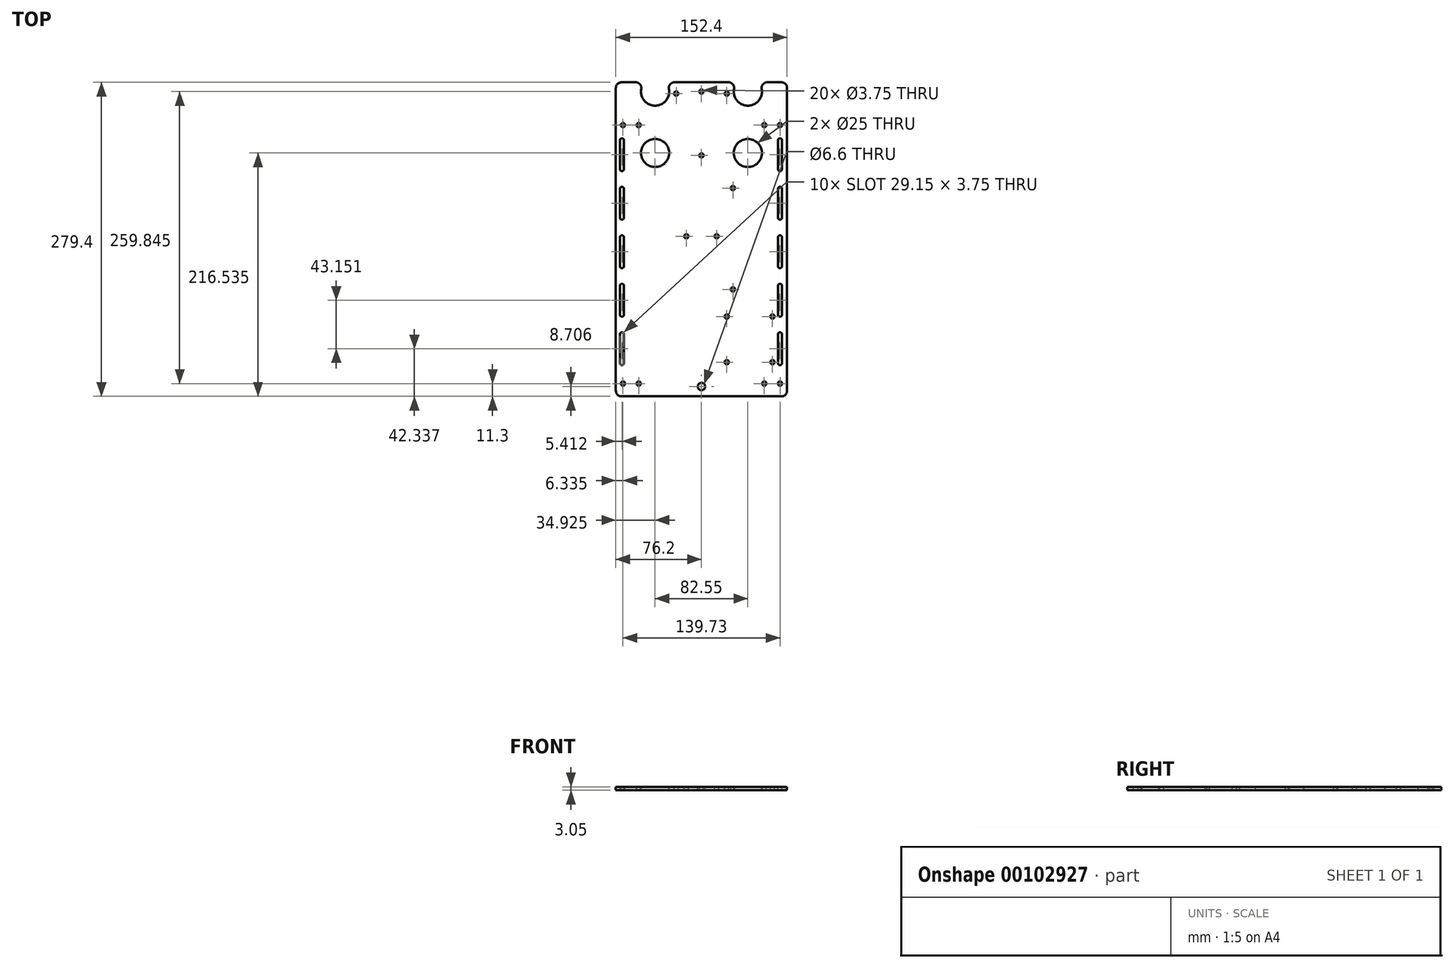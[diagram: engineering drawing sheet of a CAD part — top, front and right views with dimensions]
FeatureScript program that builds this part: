
annotation { "Feature Type Name" : "Feature", "Feature Type Description" : "" }
export const myFeature = defineFeature(function(context is Context, id is Id, definition is map)
    precondition{}
    {
        {
            var Q0;
            Q0=qCreatedBy(makeId("Top.planeOp"),FACE);
            var sketch = newSketch(context, id + "F0", { "sketchPlane" : qUnion([Q0])});
            skLineSegment(sketch, "E0.bottom", {"start": v(-76.2, 139.7) * mm, "end": v(76.2, 139.7) * mm});
            skLineSegment(sketch, "E0.top", {"start": v(-76.2, -139.7) * mm, "end": v(76.2, -139.7) * mm});
            skLineSegment(sketch, "E0.left", {"start": v(-76.2, 139.7) * mm, "end": v(-76.2, -139.7) * mm});
            skLineSegment(sketch, "E0.right", {"start": v(76.2, 139.7) * mm, "end": v(76.2, -139.7) * mm});
            skPoint(sketch, "E0.middle", {"position": v(0, 0) * mm});
            skLineSegment(sketch, "E1", {"start": v(0, 0) * mm, "end": v(0, 139.7) * mm, "construction": true});
            skLineSegment(sketch, "E2", {"start": v(-69.86, 101.6) * mm, "end": v(-55.87, 101.6) * mm, "construction": true});
            skLineSegment(sketch, "E3", {"start": v(-69.86, -128.4) * mm, "end": v(-55.86, -128.4) * mm, "construction": true});
            skLineSegment(sketch, "E4", {"start": v(27.98, 45.6) * mm, "end": v(27.98, -44.57) * mm, "construction": true});
            skLineSegment(sketch, "E5.bottom", {"start": v(-3.77, 51.31) * mm, "end": v(59.73, 51.31) * mm, "construction": true});
            skLineSegment(sketch, "E5.top", {"start": v(-3.77, -50.29) * mm, "end": v(59.73, -50.29) * mm, "construction": true});
            skLineSegment(sketch, "E5.left", {"start": v(-3.77, 51.31) * mm, "end": v(-3.77, -50.29) * mm, "construction": true});
            skLineSegment(sketch, "E5.right", {"start": v(59.73, 51.31) * mm, "end": v(59.73, -50.29) * mm, "construction": true});
            skPoint(sketch, "E5.middle", {"position": v(27.98, 0.51) * mm});
            skLineSegment(sketch, "E6.bottom", {"start": v(-68.9, 107.6) * mm, "end": v(-56.83, 107.6) * mm, "construction": true});
            skLineSegment(sketch, "E6.top", {"start": v(-68.9, 95.6) * mm, "end": v(-56.83, 95.6) * mm, "construction": true});
            skLineSegment(sketch, "E6.left", {"start": v(-68.9, 107.6) * mm, "end": v(-68.9, 95.6) * mm, "construction": true});
            skLineSegment(sketch, "E6.right", {"start": v(-56.83, 107.6) * mm, "end": v(-56.83, 95.6) * mm, "construction": true});
            skPoint(sketch, "E6.middle", {"position": v(-62.87, 101.6) * mm});
            skLineSegment(sketch, "E7.bottom", {"start": v(63.16, -109.33) * mm, "end": v(22.52, -109.33) * mm, "construction": true});
            skLineSegment(sketch, "E7.top", {"start": v(63.16, -68.7) * mm, "end": v(22.52, -68.7) * mm, "construction": true});
            skLineSegment(sketch, "E7.left", {"start": v(63.16, -109.33) * mm, "end": v(63.16, -68.7) * mm, "construction": true});
            skLineSegment(sketch, "E7.right", {"start": v(22.52, -109.33) * mm, "end": v(22.52, -68.7) * mm, "construction": true});
            skPoint(sketch, "E7.middle", {"position": v(42.84, -89.01) * mm});
            skLineSegment(sketch, "E8.MirrorCS", {"start": v(69.86, 101.6) * mm, "end": v(55.87, 101.6) * mm, "construction": true});
            skLineSegment(sketch, "E9.MirrorCS", {"start": v(69.87, -128.4) * mm, "end": v(55.87, -128.4) * mm, "construction": true});
            skLineSegment(sketch, "E10.bottom", {"start": v(-41.28, 131.44) * mm, "end": v(41.28, 131.44) * mm, "construction": true});
            skLineSegment(sketch, "E10.top", {"start": v(-41.28, 76.83) * mm, "end": v(41.27, 76.83) * mm, "construction": true});
            skLineSegment(sketch, "E10.left", {"start": v(-41.28, 131.44) * mm, "end": v(-41.28, 76.83) * mm, "construction": true});
            skLineSegment(sketch, "E10.right", {"start": v(41.28, 131.44) * mm, "end": v(41.27, 76.83) * mm, "construction": true});
            skPoint(sketch, "E10.middle", {"position": v(0, 104.14) * mm});
            skLineSegment(sketch, "E11", {"start": v(0, 131.44) * mm, "end": v(0, 74.68) * mm, "construction": true});
            skCircle(sketch, "E12", {"center": v(-41.28, 131.44) * mm, "radius": 12.5 * mm});
            skCircle(sketch, "E13", {"center": v(-41.28, 76.83) * mm, "radius": 12.5 * mm});
            skCircle(sketch, "E14", {"center": v(41.27, 76.83) * mm, "radius": 12.5 * mm});
            skCircle(sketch, "E15", {"center": v(41.28, 131.44) * mm, "radius": 12.5 * mm});
            skCircle(sketch, "E16", {"center": v(0, -131) * mm, "radius": 3.3 * mm});
            skLineSegment(sketch, "E17", {"start": v(69.85, 87.94) * mm, "end": v(69.85, 62.54) * mm, "construction": true});
            skArc(sketch, "E18.0.startCap", {"start": v(67.97, 87.94) * mm, "mid": v(69.85, 89.81) * mm, "end": v(71.72, 87.94) * mm});
            skArc(sketch, "E18.0.endCap", {"start": v(71.72, 62.54) * mm, "mid": v(69.85, 60.66) * mm, "end": v(67.97, 62.54) * mm});
            skLineSegment(sketch, "E18.0.left", {"start": v(71.72, 87.94) * mm, "end": v(71.72, 62.54) * mm});
            skLineSegment(sketch, "E18.0.right", {"start": v(67.97, 87.94) * mm, "end": v(67.97, 62.54) * mm});
            skLineSegment(sketch, "E19.0.1.0", {"start": v(71.72, 44.79) * mm, "end": v(71.72, 19.39) * mm});
            skArc(sketch, "E19.0.1.1", {"start": v(71.72, 19.39) * mm, "mid": v(69.85, 17.51) * mm, "end": v(67.97, 19.39) * mm});
            skLineSegment(sketch, "E19.0.1.2", {"start": v(67.97, 44.79) * mm, "end": v(67.97, 19.39) * mm});
            skArc(sketch, "E19.0.1.3", {"start": v(67.97, 44.79) * mm, "mid": v(69.85, 46.66) * mm, "end": v(71.72, 44.79) * mm});
            skLineSegment(sketch, "E19.0.2.0", {"start": v(71.72, 1.64) * mm, "end": v(71.72, -23.76) * mm});
            skArc(sketch, "E19.0.2.1", {"start": v(71.72, -23.76) * mm, "mid": v(69.85, -25.64) * mm, "end": v(67.97, -23.76) * mm});
            skLineSegment(sketch, "E19.0.2.2", {"start": v(67.97, 1.64) * mm, "end": v(67.97, -23.76) * mm});
            skArc(sketch, "E19.0.2.3", {"start": v(67.97, 1.64) * mm, "mid": v(69.85, 3.51) * mm, "end": v(71.72, 1.64) * mm});
            skLineSegment(sketch, "E19.0.3.0", {"start": v(71.72, -41.51) * mm, "end": v(71.72, -66.91) * mm});
            skArc(sketch, "E19.0.3.1", {"start": v(71.72, -66.91) * mm, "mid": v(69.85, -68.79) * mm, "end": v(67.97, -66.91) * mm});
            skLineSegment(sketch, "E19.0.3.2", {"start": v(67.97, -41.51) * mm, "end": v(67.97, -66.91) * mm});
            skArc(sketch, "E19.0.3.3", {"start": v(67.97, -41.51) * mm, "mid": v(69.85, -39.64) * mm, "end": v(71.72, -41.51) * mm});
            skLineSegment(sketch, "E19.0.4.0", {"start": v(71.72, -84.66) * mm, "end": v(71.72, -110.06) * mm});
            skArc(sketch, "E19.0.4.1", {"start": v(71.72, -110.06) * mm, "mid": v(69.85, -111.94) * mm, "end": v(67.97, -110.06) * mm});
            skLineSegment(sketch, "E19.0.4.2", {"start": v(67.97, -84.66) * mm, "end": v(67.97, -110.06) * mm});
            skArc(sketch, "E19.0.4.3", {"start": v(67.97, -84.66) * mm, "mid": v(69.85, -82.79) * mm, "end": v(71.72, -84.66) * mm});
            skLineSegment(sketch, "E19.1.0.0", {"start": v(-68.91, 87.94) * mm, "end": v(-68.91, 62.54) * mm});
            skArc(sketch, "E19.1.0.1", {"start": v(-68.91, 62.54) * mm, "mid": v(-70.79, 60.66) * mm, "end": v(-72.66, 62.54) * mm});
            skLineSegment(sketch, "E19.1.0.2", {"start": v(-72.66, 87.94) * mm, "end": v(-72.66, 62.54) * mm});
            skArc(sketch, "E19.1.0.3", {"start": v(-72.66, 87.94) * mm, "mid": v(-70.79, 89.81) * mm, "end": v(-68.91, 87.94) * mm});
            skLineSegment(sketch, "E19.1.1.0", {"start": v(-68.91, 44.79) * mm, "end": v(-68.91, 19.39) * mm});
            skArc(sketch, "E19.1.1.1", {"start": v(-68.91, 19.39) * mm, "mid": v(-70.79, 17.51) * mm, "end": v(-72.66, 19.39) * mm});
            skLineSegment(sketch, "E19.1.1.2", {"start": v(-72.66, 44.79) * mm, "end": v(-72.66, 19.39) * mm});
            skArc(sketch, "E19.1.1.3", {"start": v(-72.66, 44.79) * mm, "mid": v(-70.79, 46.66) * mm, "end": v(-68.91, 44.79) * mm});
            skLineSegment(sketch, "E19.1.2.0", {"start": v(-68.91, 1.64) * mm, "end": v(-68.91, -23.76) * mm});
            skArc(sketch, "E19.1.2.1", {"start": v(-68.91, -23.76) * mm, "mid": v(-70.79, -25.64) * mm, "end": v(-72.66, -23.76) * mm});
            skLineSegment(sketch, "E19.1.2.2", {"start": v(-72.66, 1.64) * mm, "end": v(-72.66, -23.76) * mm});
            skArc(sketch, "E19.1.2.3", {"start": v(-72.66, 1.64) * mm, "mid": v(-70.79, 3.51) * mm, "end": v(-68.91, 1.64) * mm});
            skLineSegment(sketch, "E19.1.3.0", {"start": v(-68.91, -41.51) * mm, "end": v(-68.91, -66.91) * mm});
            skArc(sketch, "E19.1.3.1", {"start": v(-68.91, -66.91) * mm, "mid": v(-70.79, -68.79) * mm, "end": v(-72.66, -66.91) * mm});
            skLineSegment(sketch, "E19.1.3.2", {"start": v(-72.66, -41.51) * mm, "end": v(-72.66, -66.91) * mm});
            skArc(sketch, "E19.1.3.3", {"start": v(-72.66, -41.51) * mm, "mid": v(-70.79, -39.64) * mm, "end": v(-68.91, -41.51) * mm});
            skLineSegment(sketch, "E19.1.4.0", {"start": v(-68.91, -84.66) * mm, "end": v(-68.91, -110.06) * mm});
            skArc(sketch, "E19.1.4.1", {"start": v(-68.91, -110.06) * mm, "mid": v(-70.79, -111.94) * mm, "end": v(-72.66, -110.06) * mm});
            skLineSegment(sketch, "E19.1.4.2", {"start": v(-72.66, -84.66) * mm, "end": v(-72.66, -110.06) * mm});
            skArc(sketch, "E19.1.4.3", {"start": v(-72.66, -84.66) * mm, "mid": v(-70.79, -82.79) * mm, "end": v(-68.91, -84.66) * mm});
            skLineSegment(sketch, "E19.direction1", {"start": v(67.97, 62.54) * mm, "end": v(-72.66, 62.54) * mm, "construction": true});
            skLineSegment(sketch, "E19.direction2", {"start": v(67.97, 62.54) * mm, "end": v(67.97, 19.39) * mm, "construction": true});
            skPoint(sketch, "E20.middle", {"position": v(0, -13.28) * mm});
            skLineSegment(sketch, "E21", {"start": v(-22.5, 129.7) * mm, "end": v(22.5, 129.7) * mm, "construction": true});
            skLineSegment(sketch, "E22", {"start": v(-13.5, 2.7) * mm, "end": v(13.5, 2.7) * mm, "construction": true});
            skSolve(sketch);
        }
        {
            var Q0;
            Q0=makeQuery(id+"F0.imprint","IMPRINT",FACE,{"disambiguationData":[TD([[makeQuery(id+"F0.imprint","IMPRINT",EDGE,{"derivedFrom":sQuery(id+"F0.wireOp",EDGE,"E0.top")}),1.0]])]});
            extrude(context, id + "F1", {"entities" : qUnion([Q0]), "oppositeDirection" : true, "depth" : 3.05 * mm});
        }
        {
            var Q0;
            Q0=sQuery(id+"F0.wireOp",VERTEX,"E2.start");
            var Q1;
            Q1=sQuery(id+"F0.wireOp",VERTEX,"E2.end");
            var Q2;
            Q2=sQuery(id+"F0.wireOp",VERTEX,"E4.start");
            var Q3;
            Q3=sQuery(id+"F0.wireOp",VERTEX,"E4.end");
            var Q4;
            Q4=sQuery(id+"F0.wireOp",VERTEX,"E8.MirrorCS.end");
            var Q5;
            Q5=sQuery(id+"F0.wireOp",VERTEX,"E8.MirrorCS.start");
            var Q6;
            Q6=sQuery(id+"F0.wireOp",VERTEX,"E7.top.end");
            var Q7;
            Q7=sQuery(id+"F0.wireOp",VERTEX,"E7.bottom.end");
            var Q8;
            Q8=sQuery(id+"F0.wireOp",VERTEX,"E7.bottom.start");
            var Q9;
            Q9=sQuery(id+"F0.wireOp",VERTEX,"E7.left.end");
            var Q10;
            Q10=sQuery(id+"F0.wireOp",VERTEX,"E3.end");
            var Q11;
            Q11=sQuery(id+"F0.wireOp",VERTEX,"E3.start");
            var Q12;
            Q12=sQuery(id+"F0.wireOp",VERTEX,"E9.MirrorCS.end");
            var Q13;
            Q13=sQuery(id+"F0.wireOp",VERTEX,"E9.MirrorCS.start");
            var Q14;
            Q14=sQuery(id+"F0.wireOp",VERTEX,"E11.start");
            var Q15;
            Q15=sQuery(id+"F0.wireOp",VERTEX,"E11.end");
            var Q16;
            Q16=sQuery(id+"F0.wireOp",VERTEX,"E21.start");
            var Q17;
            Q17=sQuery(id+"F0.wireOp",VERTEX,"E21.end");
            var Q18;
            Q18=sQuery(id+"F0.wireOp",VERTEX,"E22.end");
            var Q19;
            Q19=sQuery(id+"F0.wireOp",VERTEX,"E22.start");
            var Q20;
            Q20=makeQuery(id+"F1.opExtrude","SWEPT_BODY",BODY,{"disambiguationData":[OSD([sQuery(id+"F0.wireOp",EDGE,"E0.bottom"),sQuery(id+"F0.wireOp",EDGE,"E0.top"),sQuery(id+"F0.wireOp",EDGE,"E0.left"),sQuery(id+"F0.wireOp",EDGE,"E0.right")])]});
            hole(context, id + "F2", {"style" : HoleStyle.SIMPLE, "endStyle" : HoleEndStyle.THROUGH, "holeDiameter" : 3.75 * mm, "startFromSketch" : true, "locations" : qUnion([Q0, Q1, Q2, Q3, Q4, Q5, Q6, Q7, Q8, Q9, Q10, Q11, Q12, Q13, Q14, Q15, Q16, Q17, Q18, Q19]), "scope" : qUnion([Q20]), "isTappedThrough" : true});
        }
        {
            var Q0;
            Q0=makeQuery(id+"F1.opExtrude","SWEPT_EDGE",EDGE,{"disambiguationData":[OSD([sQuery(id+"F0.wireOp",EDGE,"E0.bottom"),sQuery(id+"F0.wireOp",EDGE,"E0.left")])]});
            var Q1;
            Q1=makeQuery(id+"F1.opExtrude","SWEPT_EDGE",EDGE,{"disambiguationData":[OSD([sQuery(id+"F0.wireOp",EDGE,"E0.bottom"),sQuery(id+"F0.wireOp",EDGE,"E0.right")])]});
            var Q2;
            Q2=makeQuery(id+"F1.opExtrude","SWEPT_EDGE",EDGE,{"disambiguationData":[OSD([sQuery(id+"F0.wireOp",EDGE,"E0.top"),sQuery(id+"F0.wireOp",EDGE,"E0.right")])]});
            var Q3;
            Q3=makeQuery(id+"F1.opExtrude","SWEPT_EDGE",EDGE,{"disambiguationData":[OSD([sQuery(id+"F0.wireOp",EDGE,"E0.top"),sQuery(id+"F0.wireOp",EDGE,"E0.left")])]});
            fillet(context, id + "F3", {"entities" : qUnion([Q0, Q1, Q2, Q3]), "radius" : 5.08 * mm, "tangentPropagation" : true, "allowEdgeOverflow" : false});
        }
        {
            var Q0;
            {var subQ0=sQuery(id+"F0.wireOp",EDGE,"E12");var subQ1=sQuery(id+"F0.wireOp",EDGE,"E0.bottom");Q0=makeQuery(id+"F1.opExtrude","SWEPT_EDGE",EDGE,{"disambiguationData":[OSD([subQ1,subQ0]),TDD([makeQuery(id+"F0.imprint","INTERSECT",VERTEX,{"disambiguationData":[OD(0.0)],"derivedFrom":[subQ1,subQ0]})])]});}
            var Q1;
            {var subQ0=sQuery(id+"F0.wireOp",EDGE,"E12");var subQ1=sQuery(id+"F0.wireOp",EDGE,"E0.bottom");Q1=makeQuery(id+"F1.opExtrude","SWEPT_EDGE",EDGE,{"disambiguationData":[OSD([subQ1,subQ0]),TDD([makeQuery(id+"F0.imprint","INTERSECT",VERTEX,{"disambiguationData":[OD(1.0)],"derivedFrom":[subQ1,subQ0]})])]});}
            var Q2;
            {var subQ0=sQuery(id+"F0.wireOp",EDGE,"E15");var subQ1=sQuery(id+"F0.wireOp",EDGE,"E0.bottom");Q2=makeQuery(id+"F1.opExtrude","SWEPT_EDGE",EDGE,{"disambiguationData":[OSD([subQ1,subQ0]),TDD([makeQuery(id+"F0.imprint","INTERSECT",VERTEX,{"disambiguationData":[OD(0.0)],"derivedFrom":[subQ1,subQ0]})])]});}
            var Q3;
            {var subQ0=sQuery(id+"F0.wireOp",EDGE,"E15");var subQ1=sQuery(id+"F0.wireOp",EDGE,"E0.bottom");Q3=makeQuery(id+"F1.opExtrude","SWEPT_EDGE",EDGE,{"disambiguationData":[OSD([subQ1,subQ0]),TDD([makeQuery(id+"F0.imprint","INTERSECT",VERTEX,{"disambiguationData":[OD(1.0)],"derivedFrom":[subQ1,subQ0]})])]});}
            fillet(context, id + "F4", {"entities" : qUnion([Q0, Q1, Q2, Q3]), "radius" : 5.08 * mm, "tangentPropagation" : true, "allowEdgeOverflow" : false});
        }
    });
